# Revit family: Injektionssystem VMZ, gvz
name_source: partatom
category: HLS-Bauteile
revit_build: Autodesk Revit 2017 (Build: 20190507_1515(x64)
units: mm (PartAtom-declared; Revit-internal decimal feet)

## family parameters
Basisbauteil = Fläche
Beim Laden mit Abzugskörper schneiden = Nein
Bemaßung runder Anschluss = Durchmesser verwenden
Gemeinsam genutzt = Ja
Raumberechnungspunkt = Nein
Teiletyp = Normal

## types (7) — shared parameters
Anwendungsbereich = Beton
Bohrlochtiefe = 110 mm
Brandschutz = ja
Fabrikat = MKT
Firma = MEFA Befestigungs- und Montagesysteme GmbH
Material = Stahl
Mengeneinheit = St
Oberflaeche = galvanisch verzinkt
Vorgabe-Ansicht = 1219 mm
vpe = 10 St

## per-type parameters (varying)
| type | Artikelnummer | Bohrerdurchmesser | D | EAN | Gewicht | Gewicht pro Bauteil | Gewinde | Kurztext1 | Kurztext2 | L | L1 | L2 | Länge | Länge Dübel | Mutter | Schlüsselweite | Setztiefe | Unterlegscheibe | Verankerungstiefe |
| Ankerstange VMZ-A  60 M10-10/ 85, gvz | 221832205101 | 12 mm | 8 mm  [stored 0.0262467 ft] | 4043315053381 | 0.06 kg | 0.06 kg | M10 | Ankerstange VMZ A M10 | Länge 85 mm | 85 mm  [stored 0.278871 ft] | 70 mm  [stored 0.229659 ft] | 15 mm  [stored 0.0492126 ft] | 85 mm  [stored 0.278871 ft] | 85 mm  [stored 0.278871 ft] | Sechskantmutter : Sechskantmutter M10 | 17 | 63 mm | Unterlegscheibe : Unterlegscheibe 10.5x20x2 | 60 mm |
| Ankerstange VMZ-A  80 M12-10/110, gvz | 221832305101 | 14 mm | 10 mm  [stored 0.0328084 ft] | 4043315053473 | 0.12 kg | 0.12 kg | M12 | Ankerstange VMZ A M12 | Länge 110 mm | 110 mm  [stored 0.360892 ft] | 95 mm | 15 mm  [stored 0.0492126 ft] | 110 mm  [stored 0.360892 ft] | 110 mm  [stored 0.360892 ft] | Sechskantmutter : Sechskantmutter M12 | 19 | 84 mm | Unterlegscheibe : Unterlegscheibe 13x24x2.5 | 80 mm |
| Ankerstange VMZ-A 105 M16-30/160, gvz | 221832550101 | 18 mm | 14 mm  [stored 0.0459318 ft] | 4043315065957 | 0.25 kg | 0.25 kg | M16 | Ankerstange VMZ A M16 | Länge 160 mm | 160 mm  [stored 0.524934 ft] | 140 mm  [stored 0.459318 ft] | 20 mm  [stored 0.0656168 ft] | 160 mm  [stored 0.524934 ft] | 160 mm  [stored 0.524934 ft] | Sechskantmutter : Sechskantmutter M16 | 24 | 109 mm | Unterlegscheibe : Unterlegscheibe, verstärkt 17x44x3.5 | 105 mm |
| Ankerstange VMZ-A  60 M10-60/135, gvz | 221832235101 | 12 mm | 8 mm  [stored 0.0262467 ft] | 4043315053435 | 0.09 kg | 0.09 kg | M10 | Ankerstange VMZ A M10 | Länge 135 mm | 135 mm  [stored 0.442913 ft] | 120 mm  [stored 0.393701 ft] | 15 mm  [stored 0.0492126 ft] | 135 mm  [stored 0.442913 ft] | 135 mm  [stored 0.442913 ft] | Sechskantmutter : Sechskantmutter M10 | 17 | 63 mm | Unterlegscheibe : Unterlegscheibe 10.5x20x2 | 60 mm |
| Ankerstange VMZ-A  80 M12-25/125, gvz | 221832325101 | 14 mm | 10 mm  [stored 0.0328084 ft] | 4043315053497 | 0.13 kg | 0.13 kg | M12 | Ankerstange VMZ A M12 | Länge 125 mm | 125 mm  [stored 0.410105 ft] | 110 mm  [stored 0.360892 ft] | 15 mm  [stored 0.0492126 ft] | 125 mm  [stored 0.410105 ft] | 125 mm  [stored 0.410105 ft] | Sechskantmutter : Sechskantmutter M12 | 19 | 84 mm | Unterlegscheibe : Unterlegscheibe 13x24x2.5 | 80 mm |
| Ankerstange VMZ-A 100 M12-60/180, gvz | 221832385101 | 14 mm | 10 mm  [stored 0.0328084 ft] | 4043315053596 | 0.18 kg | 0.18 kg | M12 | Ankerstange VMZ A M12 | Länge 180 mm | 180 mm  [stored 0.590551 ft] | 165 mm  [stored 0.541339 ft] | 15 mm  [stored 0.0492126 ft] | 180 mm  [stored 0.590551 ft] | 180 mm  [stored 0.590551 ft] | Sechskantmutter : Sechskantmutter M12 | 19 | 104 mm | Unterlegscheibe : Unterlegscheibe 13x24x2.5 | 100 mm |
| Ankerstange VMZ-A 125 M16-60/210, gvz | 221832520101 | 18 mm | 14 mm  [stored 0.0459318 ft] | 4043315053657 | 0.36 kg | 0.36 kg | M16 | Ankerstange VMZ A M16 | Länge 210 mm | 210 mm  [stored 0.688976 ft] | 190 mm  [stored 0.62336 ft] | 20 mm  [stored 0.0656168 ft] | 210 mm  [stored 0.688976 ft] | 210 mm  [stored 0.688976 ft] | Sechskantmutter : Sechskantmutter M16 | 24 | 130 mm | Unterlegscheibe : Unterlegscheibe, verstärkt 17x44x3.5 | 125 mm |

note: [stored X ft] marks values corroborated as IEEE doubles in the binary element streams (Revit-internal decimal feet)

## geometry (parser evidence)
native form markers: Sweep x3
no freeform markers — native parametric forms only
